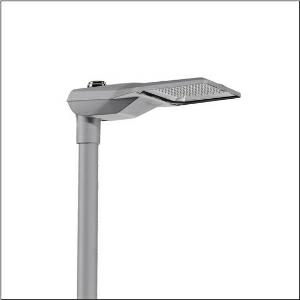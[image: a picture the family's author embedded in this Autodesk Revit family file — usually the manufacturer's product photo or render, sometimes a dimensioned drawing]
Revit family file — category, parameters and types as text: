
# Revit family: streetlight_sl_21_midi___p0_8a_5xe7u57n08mb_b7af
name_source: partatom
category: Lighting Fixtures
units: mm (PartAtom-declared; Revit-internal decimal feet)

## family parameters
Cut with Voids When Loaded = No
Host = Face
Light Source = No
Part Type = Normal
Room Calculation Point = No
Round Connector Dimension = Use Diameter
Shared = No

## types (1)
- --- (1 x LED, 15940 lm, 137 W, 3000K)
    Apparent Load = 137 VA
    CIE Flux Codes = 33 69 96 100 100
    Color Rendering = 80
    Color Temperature = 3000K
    Default Elevation = 1800 mm
    Description = Streetlight SL 21 midi, mast luminaire, primary light control with lens, of PMMA, primary optical cover: cover, of toughened safety glass, transparent, light distribution: P0.8a, light emission: direct distribution, primary light characteristic: asymmetric, installation type: side-entry, LED, 3G 2.5mm², High Power LED, rated luminous flux: 15.940lm, luminous efficacy: 116lm/W, light colour: 830, colour temperature: 3000K, control gear: NEMA (7pin), control: flexible luminous flux parameterisation, time-dependent luminous flux control, constant luminous flux control, pre-setting: linear dimming characteristic, overheat protection, mains connection: 220..240V, AC, 50/60Hz, connection cable pre-assembled, cable length: 12,5m, wiring characteristics: H05VV-F, start of lifetime: 137W, end of service life: 144W, reduction: 61W, luminaire housing, of diecast aluminium (EN AC-44300), powder-coated, SITECO metallic grey (DB 702S), corrosivity category C5 high according to DIN EN ISO 12944, multi-level sealing system, sealing non-destructively replaceable, inclination adjustable: 0°, 5°, 10°, 15°, length: 644mm, width: 335mm, height: 110mm, spigot size: 42mm (side-entry), mounting height: 4..8m, protection rating (complete): IP66, insulation class (complete): insulation class I (protective earthing), certification: CE, ENEC, ENEC+, VDE, impact resistance: IK10, permissible operating ambient temperature for outdoor applications: -40..+50°C, standard-compliant lighting for roads and squares, packaging unit: 1 piece

Light Distribution: P0.8a
    Height = 111 mm
    Lamp = 1 x LED
    Lamp Light Flux = 15940 lm
    Lamp Power = 137 W
    Lamp count = 1
    Length = 644 mm
    Luminous efficacy = 116 lm/W
    Manufacturer = Siteco
    ModVariant = No
    Model = 5XE7U57N08MB
    Number of Poles = 1
    OnlyDefault = Yes
    Power Factor = 1
    Product Name = Streetlight SL 21 midi | P0.8a
    Product group = mast luminaire | pylon top
    ProductGroupID = 6100
    Protection Class = Protection class I
    Protection Degree = IP 66
    RLX_Detail_Level = 1
    RLX_Emergency_Light_Flux = 0 lm
    RLX_Emergency_Type = 0
    RLX_Emergency_Type_DB = No
    RlxData = <blob elided: 89789 chars, md5=cf97af87>
    Socket = socket
    Standby Power = 0 W
    System Light Flux = 15940 lm
    System Power = 137 W
    Type Comments = factory setting: luminous flux: 100 % | dim-lin: 254 | 700 mA
    Type Image = l_1294377.jpg
    URL = http://relux.com
    VarID = @adj_080971
    Voltage = 0 V
    Weight = 0.00 kg
    Width = 336 mm

## geometry (parser evidence)
native form markers: Blend x4, Sweep x12
no freeform markers — native parametric forms only
